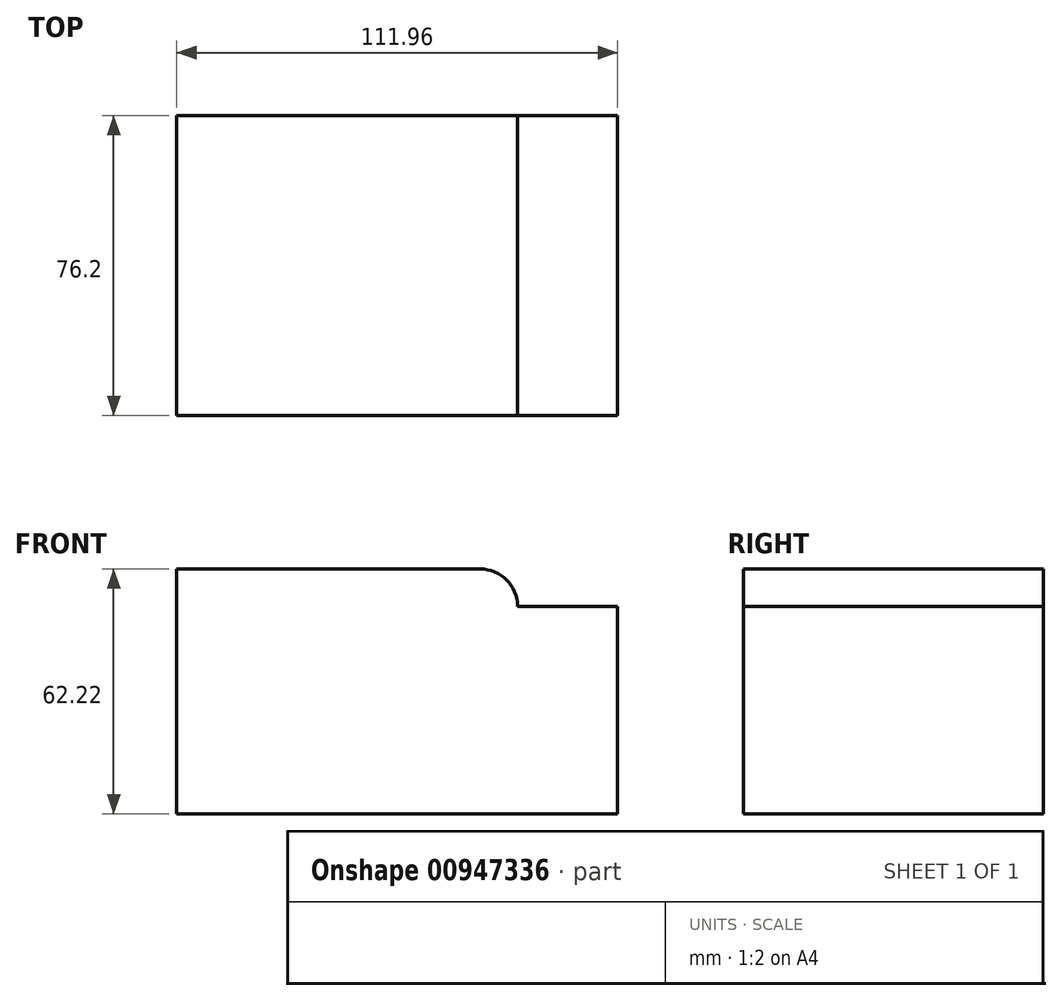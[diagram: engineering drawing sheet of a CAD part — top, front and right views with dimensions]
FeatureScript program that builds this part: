
annotation { "Feature Type Name" : "Feature", "Feature Type Description" : "" }
export const myFeature = defineFeature(function(context is Context, id is Id, definition is map)
    precondition{}
    {
        {
            var Q0;
            Q0=qCreatedBy(makeId("Front.planeOp"),FACE);
            var sketch = newSketch(context, id + "F0", { "sketchPlane" : qUnion([Q0])});
            skLineSegment(sketch, "E0.bottom", {"start": v(43.28, 31.11) * mm, "end": v(-43.28, 31.11) * mm});
            skLineSegment(sketch, "E0.top", {"start": v(43.28, -31.11) * mm, "end": v(-43.28, -31.11) * mm});
            skLineSegment(sketch, "E0.left", {"start": v(43.28, 31.11) * mm, "end": v(43.28, -31.11) * mm});
            skLineSegment(sketch, "E0.right", {"start": v(-43.28, 31.11) * mm, "end": v(-43.28, -31.11) * mm});
            skPoint(sketch, "E0.middle", {"position": v(0, 0) * mm});
            skSolve(sketch);
        }
        {
            var Q0;
            Q0 = qSketchRegion(id + "F0", true);
            extrude(context, id + "F1", {"entities" : qUnion([Q0]), "depth" : 76.2 * mm, "offsetDistance" : 25.4 * mm});
        }
        {
            var Q0;
            Q0=makeQuery(id+"F1.opExtrude","SWEPT_EDGE",EDGE,{"disambiguationData":[OSD([sQuery(id+"F0.wireOp",EDGE,"E0.bottom"),sQuery(id+"F0.wireOp",EDGE,"E0.left")])]});
            fillet(context, id + "F2", {"entities" : qUnion([Q0]), "radius" : 9.52 * mm, "tangentPropagation" : true, "allowEdgeOverflow" : false});
        }
        {
            var Q0;
            Q0=makeQuery(id+"F1.opExtrude","SWEPT_FACE",FACE,{"disambiguationData":[OSD([sQuery(id+"F0.wireOp",EDGE,"E0.left")])]});
            extrude(context, id + "F3", {"entities" : qUnion([Q0]), "operationType" : NewBodyOperationType.ADD, "depth" : 25.4 * mm, "offsetDistance" : 25.4 * mm});
        }
    });
